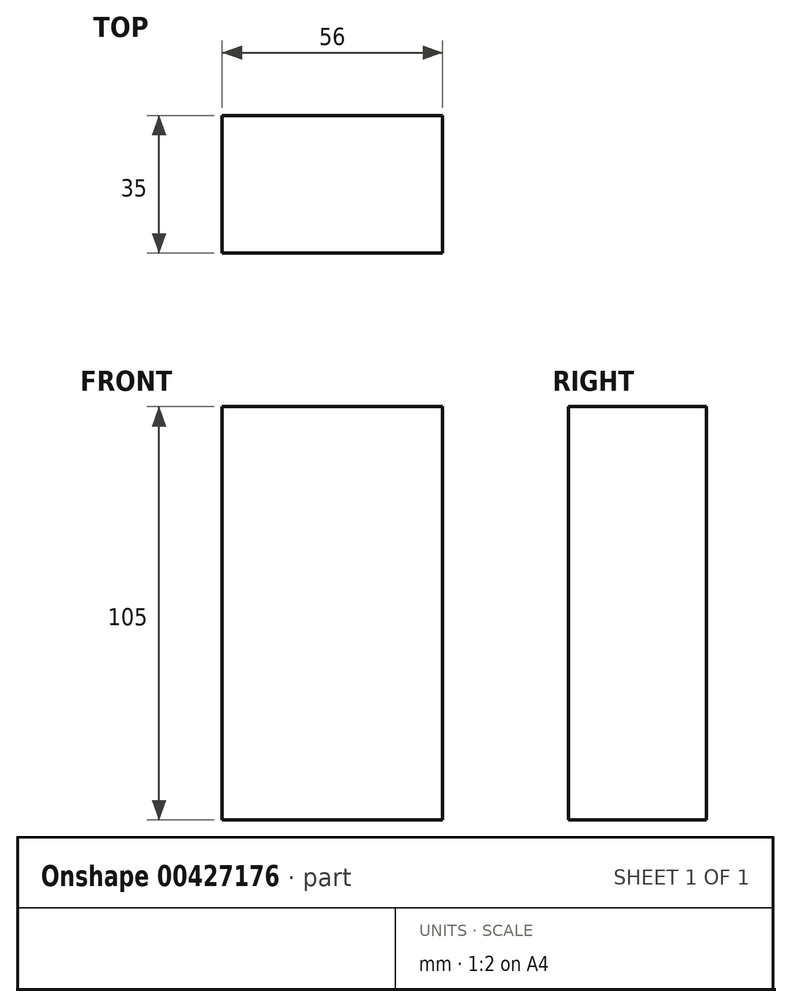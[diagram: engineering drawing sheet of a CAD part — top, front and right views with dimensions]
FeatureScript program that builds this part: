
annotation { "Feature Type Name" : "Feature", "Feature Type Description" : "" }
export const myFeature = defineFeature(function(context is Context, id is Id, definition is map)
    precondition{}
    {
        {
            var Q0;
            Q0=qCreatedBy(makeId("Right.planeOp"),FACE);
            var sketch = newSketch(context, id + "F0", { "sketchPlane" : qUnion([Q0])});
            skLineSegment(sketch, "E0", {"start": v(0, 0) * mm, "end": v(35, 0) * mm});
            skLineSegment(sketch, "E1", {"start": v(35, 0) * mm, "end": v(35, 105) * mm});
            skLineSegment(sketch, "E2", {"start": v(35, 105) * mm, "end": v(0, 105) * mm});
            skLineSegment(sketch, "E3", {"start": v(0, 105) * mm, "end": v(0, 0) * mm});
            skSolve(sketch);
        }
        {
            var Q0;
            Q0=makeQuery(id+"F0.imprint","IMPRINT",FACE,{"disambiguationData":[TD([[makeQuery(id+"F0.imprint","IMPRINT",EDGE,{"derivedFrom":sQuery(id+"F0.wireOp",EDGE,"E0")}),1.0]])]});
            extrude(context, id + "F1", {"entities" : qUnion([Q0]), "oppositeDirection" : true, "depth" : 56 * mm});
        }
    });
